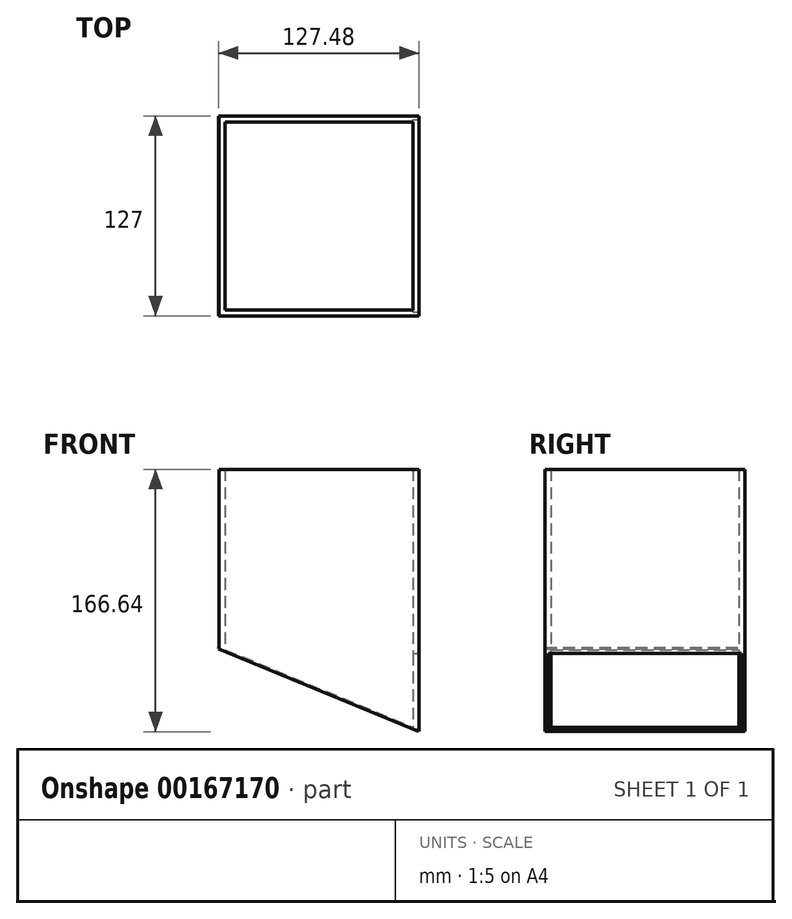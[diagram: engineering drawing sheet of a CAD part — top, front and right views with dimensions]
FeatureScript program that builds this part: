
annotation { "Feature Type Name" : "Feature", "Feature Type Description" : "" }
export const myFeature = defineFeature(function(context is Context, id is Id, definition is map)
    precondition{}
    {
        {
            var Q0;
            Q0=qCreatedBy(makeId("Top.planeOp"),FACE);
            var sketch = newSketch(context, id + "F0", { "sketchPlane" : qUnion([Q0])});
            skLineSegment(sketch, "E0", {"start": v(-63.5, 63.5) * mm, "end": v(63.5, 63.5) * mm});
            skLineSegment(sketch, "E1", {"start": v(63.5, 63.5) * mm, "end": v(63.5, -63.5) * mm});
            skLineSegment(sketch, "E2", {"start": v(63.5, -63.5) * mm, "end": v(-63.5, -63.5) * mm});
            skLineSegment(sketch, "E3", {"start": v(-63.5, -63.5) * mm, "end": v(-63.5, 63.5) * mm});
            skLineSegment(sketch, "E4", {"start": v(0, 164.54) * mm, "end": v(0, -178.78) * mm, "construction": true});
            skPoint(sketch, "E5", {"position": v(0, 63.5) * mm});
            skLineSegment(sketch, "E6", {"start": v(-114.45, 0) * mm, "end": v(129.92, 0) * mm, "construction": true});
            skPoint(sketch, "E7", {"position": v(63.5, 0) * mm});
            skLineSegment(sketch, "E8.0", {"start": v(-59.69, 59.69) * mm, "end": v(59.69, 59.69) * mm});
            skLineSegment(sketch, "E8.1", {"start": v(-59.69, -59.69) * mm, "end": v(-59.69, 59.69) * mm});
            skLineSegment(sketch, "E8.2", {"start": v(59.69, -59.7) * mm, "end": v(-59.69, -59.69) * mm});
            skLineSegment(sketch, "E8.3", {"start": v(59.7, 59.69) * mm, "end": v(59.69, -59.69) * mm});
            skSolve(sketch);
        }
        {
            var Q0;
            Q0=makeQuery(id+"F0.imprint","IMPRINT",FACE,{"disambiguationData":[TD([[makeQuery(id+"F0.imprint","IMPRINT",EDGE,{"derivedFrom":sQuery(id+"F0.wireOp",EDGE,"E0")}),-1.0]])]});
            extrude(context, id + "F1", {"entities" : qUnion([Q0]), "depth" : 177.8 * mm});
        }
        {
            var Q0;
            Q0=makeQuery(id+"FnRF2seDVqzr8Xw_1.boolean.opBoolean","MERGE",FACE,{"derivedFrom":[makeQuery(id+"F1.opExtrude","SWEPT_FACE",FACE,{"disambiguationData":[OSD([sQuery(id+"F0.wireOp",EDGE,"E2")])]}),makeQuery(id+"FnRF2seDVqzr8Xw_1.opExtrude","SWEPT_FACE",FACE,{"disambiguationData":[OSD([sQuery(id+"FozH0UINJ2bIkzI_1.wireOp",EDGE,"fb84b899-b0ee-4396-b7d4-247336cd5389.0")])]})]});
            var sketch = newSketch(context, id + "F2", { "sketchPlane" : qUnion([Q0])});
            skArc(sketch, "E9", {"start": v(50.74, 0) * mm, "mid": v(57.12, -6.38) * mm, "end": v(63.5, 0) * mm});
            skLineSegment(sketch, "E10", {"start": v(57.12, 0) * mm, "end": v(57.12, -6.38) * mm});
            skPoint(sketch, "E11", {"position": v(57.12, -3.2) * mm});
            skSolve(sketch);
        }
        {
            var Q0;
            {var subQ0=sQuery(id+"F2.wireOp",EDGE,"E9");Q0=makeQuery(id+"F2.imprint","IMPRINT",FACE,{"disambiguationData":[TD([[makeQuery(id+"F2.imprint","IMPRINT",EDGE,{"derivedFrom":subQ0}),1.0]])]});}
            extrude(context, id + "F3", {"entities" : qUnion([Q0]), "oppositeDirection" : true, "depth" : 3.8 * mm});
        }
        {
            var Q0;
            Q0=sQuery(id+"F2.wireOp",VERTEX,"E11");
            var Q1;
            Q1=makeQuery(id+"F3.opExtrude","SWEPT_BODY",BODY,{"disambiguationData":[OSD([sQuery(id+"F0.wireOp",EDGE,"E2"),sQuery(id+"F2.wireOp",EDGE,"E9")])]});
            hole(context, id + "F4", {"style" : HoleStyle.SIMPLE, "endStyle" : HoleEndStyle.BLIND, "holeDiameter" : 3.56 * mm, "holeDepth" : 2540 * mm, "locations" : qUnion([Q0]), "scope" : qUnion([Q1])});
        }
        {
            var Q0;
            Q0=makeQuery(id+"F3.opExtrude","SWEPT_BODY",BODY,{"disambiguationData":[OSD([sQuery(id+"F0.wireOp",EDGE,"E2"),sQuery(id+"F2.wireOp",EDGE,"E9")])]});
            var Q1;
            Q1=qCreatedBy(makeId("Right.planeOp"),FACE);
            mirror(context, id + "F5", {"entities" : qUnion([Q0]), "mirrorPlane" : qUnion([Q1])});
        }
        {
            var Q0;
            Q0=makeQuery(id+"F3.opExtrude","SWEPT_BODY",BODY,{"disambiguationData":[OSD([sQuery(id+"F0.wireOp",EDGE,"E2"),sQuery(id+"F2.wireOp",EDGE,"E9")])]});
            var Q1;
            Q1=qCreatedBy(makeId("Front.planeOp"),FACE);
            mirror(context, id + "F6", {"entities" : qUnion([Q0]), "mirrorPlane" : qUnion([Q1])});
        }
        {
            var Q0;
            Q0=makeQuery(id+"F5.opPattern","COPY",BODY,{"derivedFrom":makeQuery(id+"F3.opExtrude","SWEPT_BODY",BODY,{"disambiguationData":[OSD([sQuery(id+"F0.wireOp",EDGE,"E2"),sQuery(id+"F2.wireOp",EDGE,"E9")])]}),"instanceName":"1"});
            var Q1;
            Q1=qCreatedBy(makeId("Front.planeOp"),FACE);
            mirror(context, id + "F7", {"operationType" : NewBodyOperationType.ADD, "entities" : qUnion([Q0]), "mirrorPlane" : qUnion([Q1])});
        }
        {
            var Q0;
            Q0=makeQuery(id+"F1.opExtrude","SWEPT_BODY",BODY,{"disambiguationData":[OSD([sQuery(id+"F0.wireOp",EDGE,"E0"),sQuery(id+"F0.wireOp",EDGE,"E1"),sQuery(id+"F0.wireOp",EDGE,"E2"),sQuery(id+"F0.wireOp",EDGE,"E3"),sQuery(id+"F0.wireOp",EDGE,"E8.0"),sQuery(id+"F0.wireOp",EDGE,"E8.1"),sQuery(id+"F0.wireOp",EDGE,"E8.2"),sQuery(id+"F0.wireOp",EDGE,"E8.3")])]});
            var Q1;
            Q1=makeQuery(id+"F3.opExtrude","SWEPT_BODY",BODY,{"disambiguationData":[OSD([sQuery(id+"F0.wireOp",EDGE,"E2"),sQuery(id+"F2.wireOp",EDGE,"E9")])]});
            var Q2;
            Q2=makeQuery(id+"F6.opPattern","COPY",BODY,{"derivedFrom":makeQuery(id+"F3.opExtrude","SWEPT_BODY",BODY,{"disambiguationData":[OSD([sQuery(id+"F0.wireOp",EDGE,"E2"),sQuery(id+"F2.wireOp",EDGE,"E9")])]}),"instanceName":"1"});
            booleanBodies(context, id + "F8", {"operationType" : BooleanOperationType.UNION, "tools" : qUnion([Q0, Q1, Q2])});
        }
        {
            var Q0;
            {var subQ0=sQuery(id+"F0.wireOp",EDGE,"E2");Q0=makeQuery(id+"F2.imprint","IMPRINT",FACE,{"disambiguationData":[TD([[makeQuery(id+"F2.imprint","IMPRINT",EDGE,{"derivedFrom":makeQuery(id+"F1.opExtrude","CAP_EDGE",EDGE,{"disambiguationData":[OSD([subQ0])],"isStart":false})}),1.0]])]});}
            var sketch = newSketch(context, id + "F9", { "sketchPlane" : qUnion([Q0])});
            skLineSegment(sketch, "E12", {"start": v(93.37, 0) * mm, "end": v(-89.88, 75.68) * mm});
            skLineSegment(sketch, "E13", {"start": v(-89.88, 75.68) * mm, "end": v(-89.88, -21.48) * mm});
            skLineSegment(sketch, "E14", {"start": v(-89.88, -21.48) * mm, "end": v(75.67, -13.25) * mm});
            skLineSegment(sketch, "E15", {"start": v(93.37, 0) * mm, "end": v(75.67, -13.25) * mm});
            skSolve(sketch);
        }
        {
            var Q0;
            Q0 = qSketchRegion(id + "F9", true);
            extrude(context, id + "F10", {"entities" : qUnion([Q0]), "operationType" : NewBodyOperationType.REMOVE, "endBound" : BoundingType.THROUGH_ALL, "oppositeDirection" : true, "depth" : 25.4 * mm});
        }
        {
            var Q0;
            Q0=makeQuery(id+"F10.boolean.opBoolean","COPY",FACE,{"derivedFrom":makeQuery(id+"F10.opExtrude","SWEPT_FACE",FACE,{"disambiguationData":[OSD([sQuery(id+"F9.wireOp",EDGE,"E12")])]})});
            var sketch = newSketch(context, id + "F11", { "sketchPlane" : qUnion([Q0])});
            skLineSegment(sketch, "E16.0", {"start": v(-83.42, -63.5) * mm, "end": v(53.98, -63.5) * mm});
            skLineSegment(sketch, "E17.0", {"start": v(53.98, -63.5) * mm, "end": v(53.98, 63.5) * mm});
            skLineSegment(sketch, "E18.0", {"start": v(53.98, 63.5) * mm, "end": v(-83.42, 63.5) * mm});
            skLineSegment(sketch, "E19.0", {"start": v(-83.42, 63.5) * mm, "end": v(-83.42, -63.5) * mm});
            skSolve(sketch);
        }
        {
            var Q0;
            Q0 = qSketchRegion(id + "F11", true);
            extrude(context, id + "F12", {"entities" : qUnion([Q0]), "operationType" : NewBodyOperationType.ADD, "depth" : 1.27 * mm});
        }
        {
            var Q0;
            Q0=makeQuery(id+"F1.opExtrude","SWEPT_FACE",FACE,{"disambiguationData":[OSD([sQuery(id+"F0.wireOp",EDGE,"E1")])]});
            var sketch = newSketch(context, id + "F13", { "sketchPlane" : qUnion([Q0])});
            skLineSegment(sketch, "E20.0", {"start": v(-63.5, 63.14) * mm, "end": v(-63.5, 12.34) * mm});
            skLineSegment(sketch, "E21.0", {"start": v(63.5, 12.34) * mm, "end": v(-63.5, 12.34) * mm});
            skLineSegment(sketch, "E22.0", {"start": v(63.5, 63.14) * mm, "end": v(63.5, 12.34) * mm});
            skLineSegment(sketch, "E23", {"start": v(-63.5, 63.14) * mm, "end": v(63.5, 63.14) * mm});
            skPoint(sketch, "E24.orphan", {"position": v(-63.5, 177.8) * mm});
            skPoint(sketch, "E25.orphan", {"position": v(63.5, 177.8) * mm});
            skLineSegment(sketch, "E26.0", {"start": v(-61.21, 60.85) * mm, "end": v(-61.21, 12.84) * mm});
            skLineSegment(sketch, "E26.1", {"start": v(-61.21, 60.85) * mm, "end": v(61.21, 60.85) * mm});
            skLineSegment(sketch, "E26.2", {"start": v(61.21, 60.85) * mm, "end": v(61.21, 12.84) * mm});
            skLineSegment(sketch, "E26.3", {"start": v(61.21, 12.84) * mm, "end": v(-61.21, 12.84) * mm});
            skSolve(sketch);
        }
        {
            var Q0;
            Q0=makeQuery(id+"F13.imprint","IMPRINT",FACE,{"disambiguationData":[TD([[makeQuery(id+"F13.imprint","IMPRINT",EDGE,{"derivedFrom":sQuery(id+"F13.wireOp",EDGE,"E26.0")}),1.0]])]});
            extrude(context, id + "F14", {"entities" : qUnion([Q0]), "operationType" : NewBodyOperationType.REMOVE, "oppositeDirection" : true, "depth" : 3.8 * mm});
        }
    });
